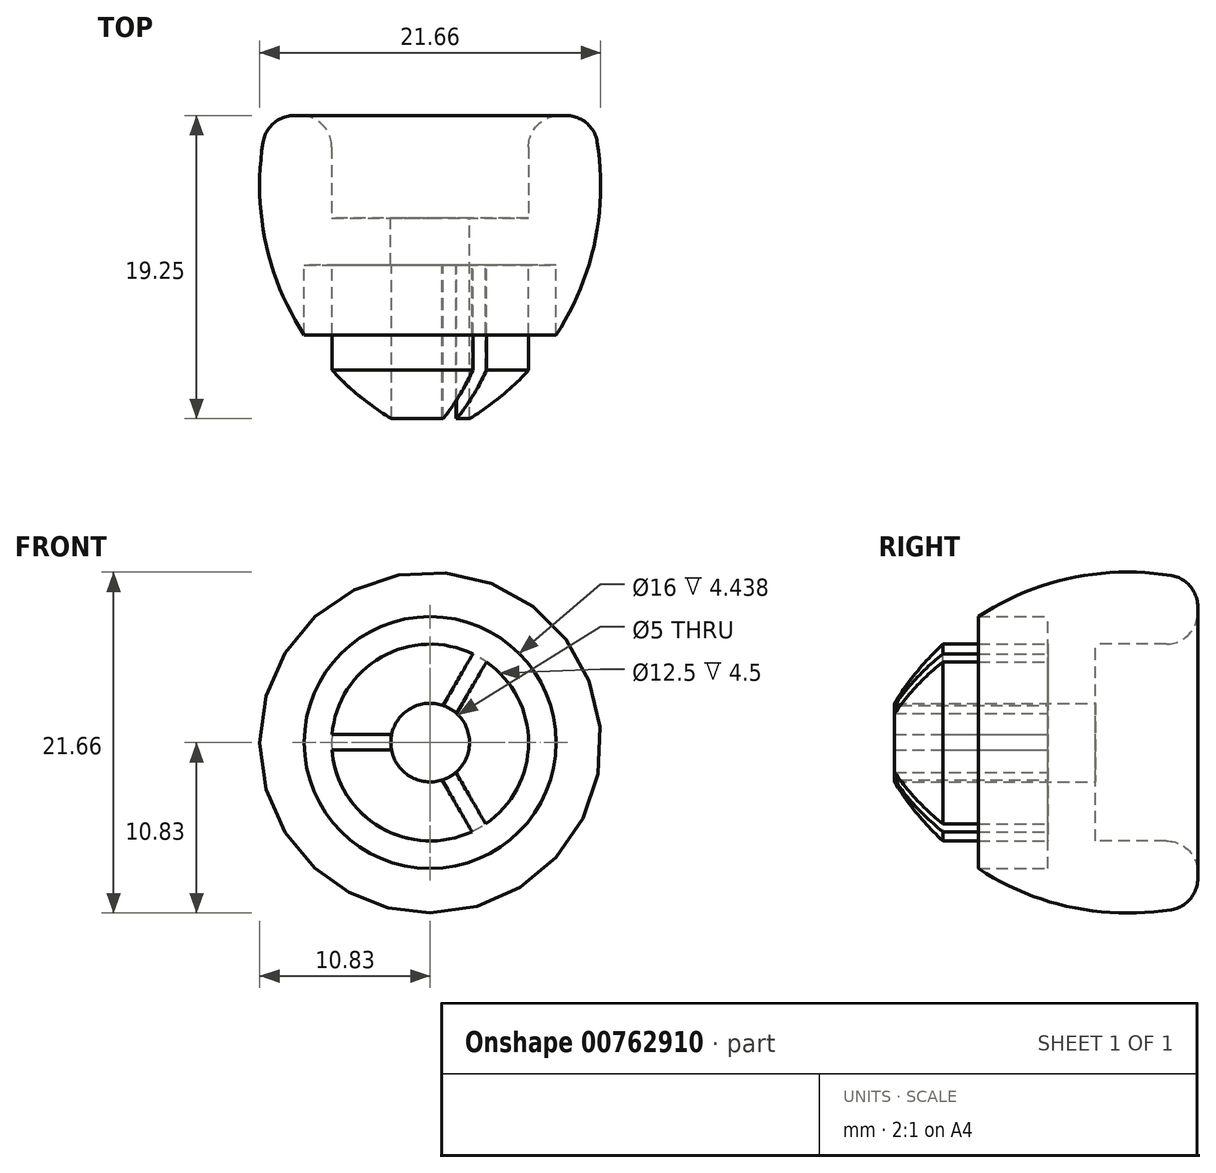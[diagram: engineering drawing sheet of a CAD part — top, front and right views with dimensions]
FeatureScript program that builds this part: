
annotation { "Feature Type Name" : "Feature", "Feature Type Description" : "" }
export const myFeature = defineFeature(function(context is Context, id is Id, definition is map)
    precondition{}
    {
        {
            var Q0;
            Q0=qCreatedBy(makeId("Front.planeOp"),FACE);
            var sketch = newSketch(context, id + "F0", { "sketchPlane" : qUnion([Q0])});
            skCircle(sketch, "E0", {"center": v(0, 0) * mm, "radius": 6.25 * mm});
            skCircle(sketch, "E1", {"center": v(0, 0) * mm, "radius": 8 * mm});
            skCircle(sketch, "E2", {"center": v(0, 0) * mm, "radius": 2.5 * mm});
            skSolve(sketch);
        }
        {
            var Q0;
            Q0=qCreatedBy(makeId("Front.planeOp"),FACE);
            var sketch = newSketch(context, id + "F1", { "sketchPlane" : qUnion([Q0])});
            skLineSegment(sketch, "E3.bottom", {"start": v(-7, 0.53) * mm, "end": v(-1, 0.53) * mm});
            skLineSegment(sketch, "E3.top", {"start": v(-7, -0.47) * mm, "end": v(-1, -0.47) * mm});
            skLineSegment(sketch, "E3.left", {"start": v(-7, 0.53) * mm, "end": v(-7, -0.47) * mm});
            skLineSegment(sketch, "E3.right", {"start": v(-1, 0.53) * mm, "end": v(-1, -0.47) * mm});
            skLineSegment(sketch, "E4.1.0", {"start": v(3.04, -6.33) * mm, "end": v(0.04, -1.13) * mm});
            skLineSegment(sketch, "E4.1.1", {"start": v(0.04, -1.13) * mm, "end": v(0.9, -0.63) * mm});
            skLineSegment(sketch, "E4.1.2", {"start": v(3.9, -5.83) * mm, "end": v(0.9, -0.63) * mm});
            skLineSegment(sketch, "E4.1.3", {"start": v(3.04, -6.33) * mm, "end": v(3.9, -5.83) * mm});
            skLineSegment(sketch, "E4.2.0", {"start": v(3.96, 5.8) * mm, "end": v(0.96, 0.6) * mm});
            skLineSegment(sketch, "E4.2.1", {"start": v(0.96, 0.6) * mm, "end": v(0.1, 1.1) * mm});
            skLineSegment(sketch, "E4.2.2", {"start": v(3.1, 6.3) * mm, "end": v(0.1, 1.1) * mm});
            skLineSegment(sketch, "E4.2.3", {"start": v(3.96, 5.8) * mm, "end": v(3.1, 6.3) * mm});
            skPoint(sketch, "E4.center", {"position": v(0, 0) * mm});
            skSolve(sketch);
        }
        {
            var Q0;
            Q0=qCreatedBy(makeId("Right.planeOp"),FACE);
            var sketch = newSketch(context, id + "F2", { "sketchPlane" : qUnion([Q0])});
            skArc(sketch, "E5", {"start": v(9.5, 10.25) * mm, "mid": v(-2.7, 9) * mm, "end": v(-11, 0) * mm});
            skLineSegment(sketch, "E6", {"start": v(9.5, 10.25) * mm, "end": v(9.5, 0) * mm});
            skLineSegment(sketch, "E7", {"start": v(9.5, 0) * mm, "end": v(-11, 0) * mm});
            skSolve(sketch);
        }
        {
            var Q0;
            Q0 = qSketchRegion(id + "F2", true);
            var Q1;
            Q1=sQuery(id+"F2.wireOp",EDGE,"E7");
            revolve(context, id + "F3", {"surfaceOperationType" : NewSurfaceOperationType.NEW, "entities" : qUnion([Q0]), "axis" : qUnion([Q1]), "revolveType" : RevolveType.FULL});
        }
        {
            var Q0;
            Q0 = qSketchRegion(id + "F0", true);
            var Q1;
            Q1=sQuery(id+"F0.wireOp",EDGE,"E1");
            extrude(context, id + "F4", {"entities" : qUnion([Q0]), "operationType" : NewBodyOperationType.REMOVE, "surfaceEntities" : qUnion([Q1]), "depth" : 25 * mm, "offsetDistance" : 25 * mm});
        }
        {
            var Q0;
            Q0=makeQuery(id+"F0.imprint","IMPRINT",FACE,{"disambiguationData":[TD([[makeQuery(id+"F0.imprint","IMPRINT",EDGE,{"derivedFrom":sQuery(id+"F0.wireOp",EDGE,"E2")}),1.0]])]});
            extrude(context, id + "F5", {"entities" : qUnion([Q0]), "operationType" : NewBodyOperationType.REMOVE, "depth" : 20 * mm, "offsetDistance" : 25 * mm, "hasSecondDirection" : true, "secondDirectionOppositeDirection" : true, "secondDirectionDepth" : 4 * mm});
        }
        {
            var Q0;
            Q0=makeQuery(id+"F0.imprint","IMPRINT",FACE,{"disambiguationData":[TD([[makeQuery(id+"F0.imprint","IMPRINT",EDGE,{"derivedFrom":sQuery(id+"F0.wireOp",EDGE,"E0")}),1.0]])]});
            var Q1;
            Q1=makeQuery(id+"F0.imprint","IMPRINT",FACE,{"disambiguationData":[TD([[makeQuery(id+"F0.imprint","IMPRINT",EDGE,{"derivedFrom":sQuery(id+"F0.wireOp",EDGE,"E2")}),1.0]])]});
            extrude(context, id + "F6", {"entities" : qUnion([Q0, Q1]), "operationType" : NewBodyOperationType.REMOVE, "endBound" : BoundingType.THROUGH_ALL, "oppositeDirection" : true, "depth" : 25 * mm, "offsetDistance" : 25 * mm, "hasSecondDirection" : true, "secondDirectionOppositeDirection" : true, "secondDirectionDepth" : 3 * mm});
        }
        {
            var Q0;
            Q0 = qSketchRegion(id + "F1", true);
            extrude(context, id + "F7", {"entities" : qUnion([Q0]), "operationType" : NewBodyOperationType.REMOVE, "depth" : 25 * mm, "offsetDistance" : 25 * mm});
        }
        {
            var Q0;
            Q0=makeQuery(id+"F3.opRevolve","SWEPT_EDGE",EDGE,{"disambiguationData":[OSD([sQuery(id+"F2.wireOp",EDGE,"E5"),sQuery(id+"F2.wireOp",EDGE,"E6")])]});
            var Q1;
            Q1=makeQuery(id+"F6.boolean.opBoolean","INTERSECT",EDGE,{"derivedFrom":[makeQuery(id+"F3.opRevolve","SWEPT_FACE",FACE,{"disambiguationData":[OSD([sQuery(id+"F2.wireOp",EDGE,"E6")])]}),makeQuery(id+"F6.opExtrude","SWEPT_FACE",FACE,{"disambiguationData":[OSD([sQuery(id+"F0.wireOp",EDGE,"E0")])]})]});
            fillet(context, id + "F8", {"entities" : qUnion([Q0, Q1]), "radius" : 2 * mm, "tangentPropagation" : true, "allowEdgeOverflow" : false});
        }
    });
